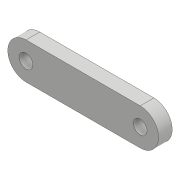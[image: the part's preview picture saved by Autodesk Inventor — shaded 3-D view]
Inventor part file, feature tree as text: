
AUTODESK INVENTOR PART (.ipt)
format: ipt  version: 2018 (Build 220112000, 112)  size: 87,552 bytes
history: native  units: mm
features: extrude x1, sketch x1
ambient origin geometry x8: Origin, YZ Plane, XZ Plane, XY Plane, X Axis, Y Axis, Z Axis, Center Point
bodies: Solid1 (feature_tree)
feature tree (2):
  extrude  "Extrusion1"  Depth=8.0mm
  sketch  "Sketch1"  dims[d0=3.0mm d1=8.0mm d4=25.0mm d5=8.0mm d6=3.0mm d7=3.0mm d8=0.0mm]
